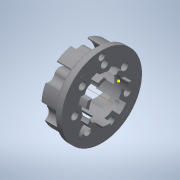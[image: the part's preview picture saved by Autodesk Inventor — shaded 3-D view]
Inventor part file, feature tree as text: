
AUTODESK INVENTOR PART (.ipt)
format: ipt  version: 2020 (Build 240168000, 168)  size: 677,376 bytes
history: native  units: in
note: dims shown in document units (in); Inventor stores cm internally (conversion verified against a paired STEP export)
features: sketch x19, other x4, extrude x4, plane x2
ambient origin geometry x8: Origin, YZ Plane, XZ Plane, XY Plane, X Axis, Y Axis, Z Axis, Center Point
bodies: Solid1 (feature_tree)
feature tree (29):
  other  "Mecanum Adaptor 1.3.ipt"
  extrude  "Extrusion1"  Depth=0.1575in
  extrude  "Extrusion2"  Depth=0.1406in
  extrude  "Extrusion3"  Depth=0.157in TaperAngle=0.0deg
  extrude  "Extrusion4"  [1 undecoded]
  sketch  "Sketch22"
  other  "Solid1::Mecanum Adaptor 1.3.ipt"
  other  "TaggingFeature1"
  sketch  "Sketch1"  dims[d0=0.3937in]
  sketch  "Sketch3"  dims[d4=0.4724in d5=0.0in d6=0.0787in d7=1.757in d8=1.6061in d9=0.0in d10=90.0deg d11=0.0in d12=90.0deg d13=0.1181in d14=0.0in d15=0.1575in d16=2.7559in d21=0.0in d23=0.0in d25=0.0in d26=0.1575in d27=0.0in d28=0.374in d29=2.7559in d33=0.0787in d34=0.0in d35=0.1378in d36=0.0in d38=0.0in d55=2.7559in d60=0.0in d61=0.2756in d62=0.7874in d64=0.446in d65=0.7874in d67=0.446in d70=0.0984in d71=0.0in d72=0.2638in d73=0.1575in d75=0.2638in d76=0.1575in d78=0.2638in d79=0.1575in d81=0.2638in d82=0.1575in d84=0.2638in d85=0.1575in d87=0.2638in d88=0.1575in d90=0.2638in d91=0.1575in d93=0.1575in d2=360.0deg d18=360.0deg d31=360.0deg d57=360.0deg d1=0.875in]
  sketch  "Sketch4"  dims[d3=1.0in d17=0.0in d19=0.1406in]
  sketch  "Sketch5"  dims[d20=1.0in d22=0.0in d24=0.157in d30=0.0in]
  sketch  "Sketch6"  dims[d32=0.158in d37=0.0in]
  sketch  "Sketch7"
  sketch  "Sketch8"
  sketch  "Sketch9"
  sketch  "Sketch10"
  sketch  "Sketch11"
  sketch  "Sketch12"
  sketch  "Sketch14"
  sketch  "Sketch16"
  sketch  "Sketch17"
  plane  "Work Plane1"
  plane  "Work Plane2"
  other  "Work Axis1"
  sketch  "Sketch18"
  sketch  "Sketch19"
  sketch  "Sketch20"
  sketch  "Sketch21"
note: 1 required parameter value undecoded (feature->parameter linkage not recoverable at this tier; creation-order binding heuristic only, values carry confidence <= 0.55)
